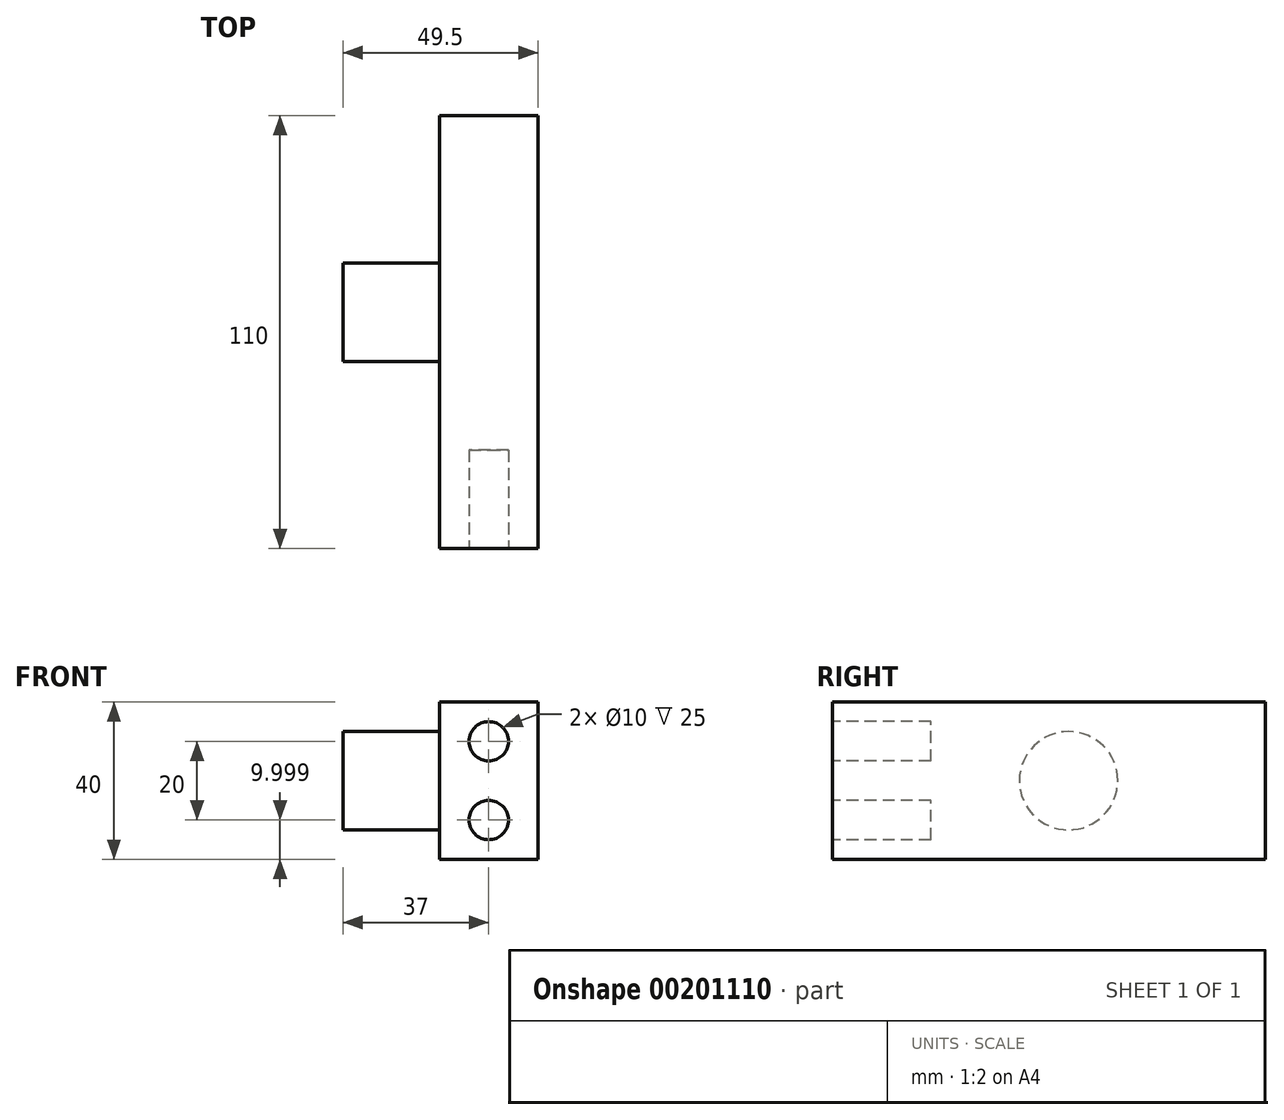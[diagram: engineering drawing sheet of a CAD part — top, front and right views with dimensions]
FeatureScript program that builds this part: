
annotation { "Feature Type Name" : "Feature", "Feature Type Description" : "" }
export const myFeature = defineFeature(function(context is Context, id is Id, definition is map)
    precondition{}
    {
        {
            var Q0;
            Q0=qCreatedBy(makeId("Right.planeOp"),FACE);
            var sketch = newSketch(context, id + "F0", { "sketchPlane" : qUnion([Q0])});
            skLineSegment(sketch, "E0.bottom", {"start": v(-55, -24.4) * mm, "end": v(55, -24.4) * mm});
            skLineSegment(sketch, "E0.top", {"start": v(-55, 15.6) * mm, "end": v(55, 15.6) * mm});
            skLineSegment(sketch, "E0.left", {"start": v(-55, -24.4) * mm, "end": v(-55, 15.6) * mm});
            skLineSegment(sketch, "E0.right", {"start": v(55, -24.4) * mm, "end": v(55, 15.6) * mm});
            skPoint(sketch, "E0.middle", {"position": v(0, -4.4) * mm});
            skSolve(sketch);
        }
        {
            var Q0;
            Q0 = qSketchRegion(id + "F0", true);
            extrude(context, id + "F1", {"entities" : qUnion([Q0]), "depth" : 25 * mm});
        }
        {
            var Q0;
            Q0=makeQuery(id+"F1.opExtrude","CAP_FACE",FACE,{"disambiguationData":[OSD([sQuery(id+"F0.wireOp",EDGE,"E0.bottom"),sQuery(id+"F0.wireOp",EDGE,"E0.top"),sQuery(id+"F0.wireOp",EDGE,"E0.left"),sQuery(id+"F0.wireOp",EDGE,"E0.right")])],"isStart":true});
            var sketch = newSketch(context, id + "F2", { "sketchPlane" : qUnion([Q0])});
            skCircle(sketch, "E1", {"center": v(-5, -4.4) * mm, "radius": 12.5 * mm});
            skPoint(sketch, "E1.centerSnap0", {"position": v(-55, -4.4) * mm});
            skSolve(sketch);
        }
        {
            var Q0;
            Q0 = qSketchRegion(id + "F2", true);
            extrude(context, id + "F3", {"entities" : qUnion([Q0]), "operationType" : NewBodyOperationType.ADD, "depth" : 24.5 * mm});
        }
        {
            var Q0;
            Q0=makeQuery(id+"F1.opExtrude","SWEPT_FACE",FACE,{"disambiguationData":[OSD([sQuery(id+"F0.wireOp",EDGE,"E0.left")])]});
            var sketch = newSketch(context, id + "F4", { "sketchPlane" : qUnion([Q0])});
            skCircle(sketch, "E2", {"center": v(12.5, 5.6) * mm, "radius": 5 * mm});
            skPoint(sketch, "E2.centerSnap0", {"position": v(12.5, 15.6) * mm});
            skCircle(sketch, "E3", {"center": v(12.5, -14.4) * mm, "radius": 5 * mm});
            skPoint(sketch, "E3.centerSnap0", {"position": v(12.5, -24.4) * mm});
            skSolve(sketch);
        }
        {
            var Q0;
            Q0=makeQuery(id+"F4.imprint","IMPRINT",FACE,{"disambiguationData":[TD([[makeQuery(id+"F4.imprint","IMPRINT",EDGE,{"derivedFrom":sQuery(id+"F4.wireOp",EDGE,"E2")}),1.0]])]});
            extrude(context, id + "F5", {"entities" : qUnion([Q0]), "operationType" : NewBodyOperationType.REMOVE, "oppositeDirection" : true, "depth" : 25 * mm});
        }
        {
            var Q0;
            Q0 = qSketchRegion(id + "F4", true);
            extrude(context, id + "F6", {"entities" : qUnion([Q0]), "operationType" : NewBodyOperationType.REMOVE, "oppositeDirection" : true, "depth" : 25 * mm});
        }
    });
